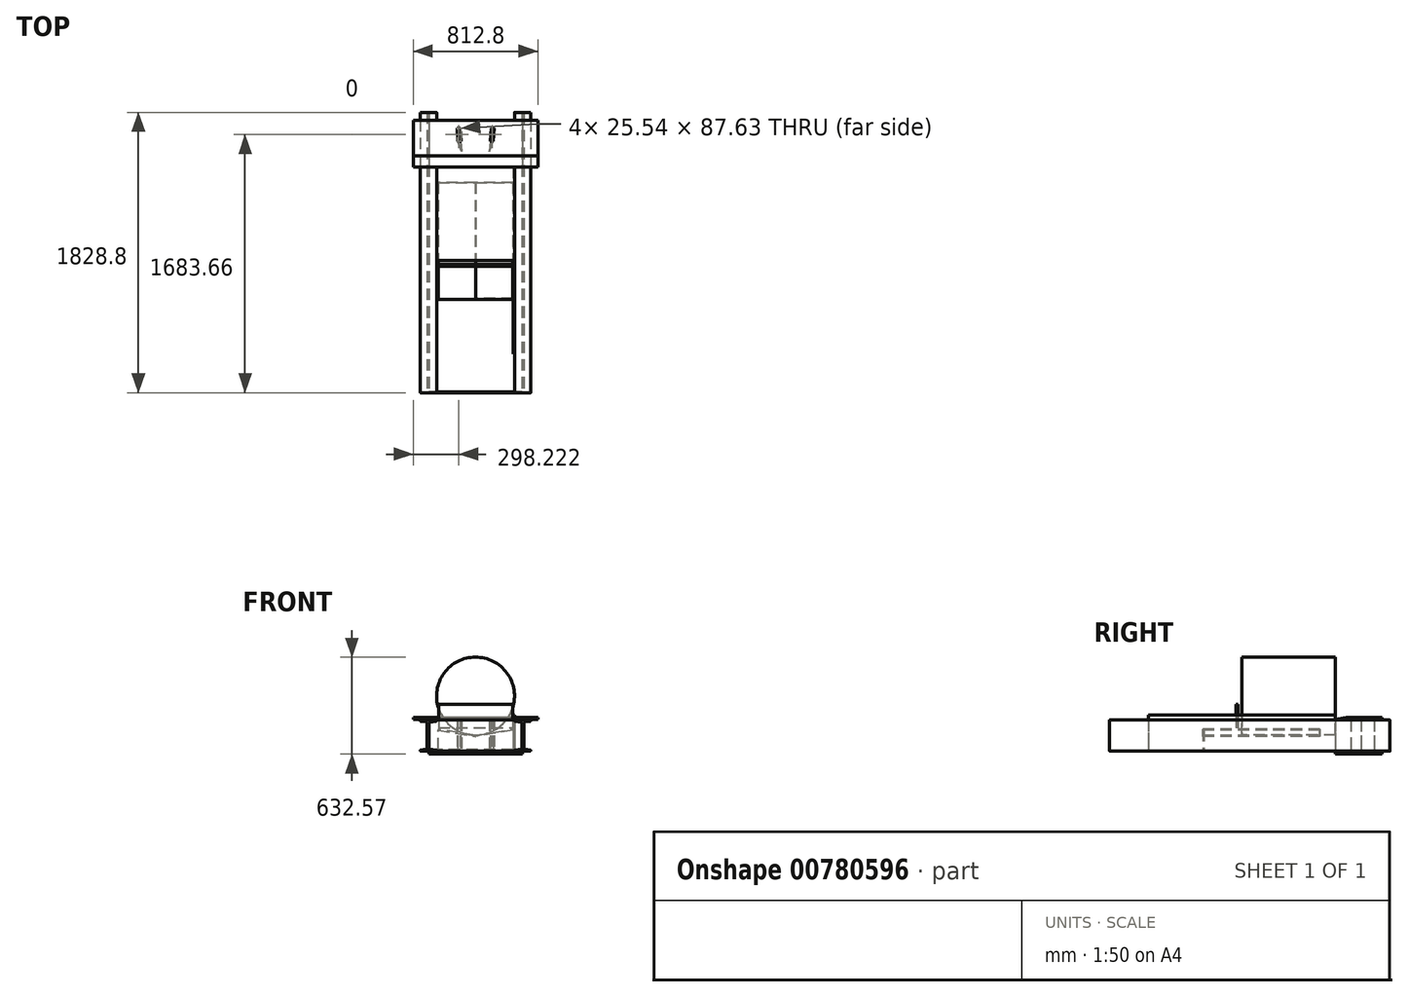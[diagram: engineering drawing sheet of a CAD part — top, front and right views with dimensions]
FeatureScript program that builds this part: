
annotation { "Feature Type Name" : "Feature", "Feature Type Description" : "" }
export const myFeature = defineFeature(function(context is Context, id is Id, definition is map)
    precondition{}
    {
        {
            var Q0;
            Q0=qCreatedBy(makeId("Front.planeOp"),FACE);
            var sketch = newSketch(context, id + "F0", { "sketchPlane" : qUnion([Q0])});
            skLineSegment(sketch, "E0", {"start": v(-357.5, -203.2) * mm, "end": v(-257.18, -203.2) * mm});
            skLineSegment(sketch, "E1", {"start": v(-357.5, 0) * mm, "end": v(-257.18, 0) * mm});
            skLineSegment(sketch, "E2", {"start": v(-360.68, -3.18) * mm, "end": v(-360.68, -5.19) * mm});
            skLineSegment(sketch, "E3", {"start": v(-254, -3.18) * mm, "end": v(-254, -5.15) * mm});
            skLineSegment(sketch, "E4", {"start": v(-256.76, -8.3) * mm, "end": v(-296.95, -13.6) * mm});
            skLineSegment(sketch, "E5", {"start": v(-303.86, -21.46) * mm, "end": v(-303.86, -181.82) * mm});
            skLineSegment(sketch, "E6", {"start": v(-297.05, -189.68) * mm, "end": v(-256.72, -195.5) * mm});
            skLineSegment(sketch, "E7", {"start": v(-254, -198.63) * mm, "end": v(-254, -200.03) * mm});
            skLineSegment(sketch, "E8", {"start": v(-360.68, -200.03) * mm, "end": v(-360.68, -198.6) * mm});
            skLineSegment(sketch, "E9", {"start": v(-358, -195.46) * mm, "end": v(-321.83, -189.76) * mm});
            skLineSegment(sketch, "E10", {"start": v(-315.13, -181.92) * mm, "end": v(-315.13, -21.38) * mm});
            skLineSegment(sketch, "E11", {"start": v(-321.94, -13.52) * mm, "end": v(-357.96, -8.33) * mm});
            skPoint(sketch, "E12.visualSharp", {"position": v(-360.68, -7.94) * mm});
            skArc(sketch, "E12.filletArc", {"start": v(-360.68, -5.19) * mm, "mid": v(-359.9, -7.27) * mm, "end": v(-357.96, -8.33) * mm});
            skPoint(sketch, "E13.visualSharp", {"position": v(-360.68, -195.88) * mm});
            skArc(sketch, "E13.filletArc", {"start": v(-358, -195.46) * mm, "mid": v(-359.92, -196.53) * mm, "end": v(-360.68, -198.6) * mm});
            skPoint(sketch, "E14.visualSharp", {"position": v(-254, -7.94) * mm});
            skArc(sketch, "E14.filletArc", {"start": v(-256.76, -8.3) * mm, "mid": v(-254.79, -7.25) * mm, "end": v(-254, -5.15) * mm});
            skPoint(sketch, "E15.visualSharp", {"position": v(-254, -195.88) * mm});
            skArc(sketch, "E15.filletArc", {"start": v(-254, -198.63) * mm, "mid": v(-254.78, -196.55) * mm, "end": v(-256.72, -195.5) * mm});
            skPoint(sketch, "E16.visualSharp", {"position": v(-254, -203.2) * mm});
            skArc(sketch, "E16.filletArc", {"start": v(-257.18, -203.2) * mm, "mid": v(-254.93, -202.27) * mm, "end": v(-254, -200.03) * mm});
            skPoint(sketch, "E17.visualSharp", {"position": v(-360.68, -203.2) * mm});
            skArc(sketch, "E17.filletArc", {"start": v(-360.68, -200.03) * mm, "mid": v(-359.75, -202.27) * mm, "end": v(-357.5, -203.2) * mm});
            skPoint(sketch, "E18.visualSharp", {"position": v(-360.68, 0) * mm});
            skArc(sketch, "E18.filletArc", {"start": v(-357.5, 0) * mm, "mid": v(-359.75, -0.93) * mm, "end": v(-360.68, -3.18) * mm});
            skPoint(sketch, "E19.visualSharp", {"position": v(-254, 0) * mm});
            skArc(sketch, "E19.filletArc", {"start": v(-254, -3.18) * mm, "mid": v(-254.93, -0.93) * mm, "end": v(-257.18, 0) * mm});
            skPoint(sketch, "E20.visualSharp", {"position": v(-303.86, -14.5) * mm});
            skArc(sketch, "E20.filletArc", {"start": v(-296.95, -13.6) * mm, "mid": v(-301.89, -16.23) * mm, "end": v(-303.86, -21.46) * mm});
            skPoint(sketch, "E21.visualSharp", {"position": v(-315.13, -14.5) * mm});
            skArc(sketch, "E21.filletArc", {"start": v(-315.13, -21.38) * mm, "mid": v(-317.07, -16.18) * mm, "end": v(-321.94, -13.52) * mm});
            skPoint(sketch, "E22.visualSharp", {"position": v(-303.86, -188.7) * mm});
            skArc(sketch, "E22.filletArc", {"start": v(-303.86, -181.82) * mm, "mid": v(-301.92, -187.02) * mm, "end": v(-297.05, -189.68) * mm});
            skPoint(sketch, "E23.visualSharp", {"position": v(-315.13, -188.7) * mm});
            skArc(sketch, "E23.filletArc", {"start": v(-321.83, -189.76) * mm, "mid": v(-317.04, -187.07) * mm, "end": v(-315.13, -181.92) * mm});
            skSolve(sketch);
        }
        {
            var Q0;
            Q0 = qSketchRegion(id + "F0", true);
            extrude(context, id + "F1", {"entities" : qUnion([Q0]), "oppositeDirection" : true, "depth" : 1828.8 * mm, "offsetDistance" : 25.4 * mm});
        }
        {
            var Q0;
            Q0=makeQuery(id+"F1.opExtrude","SWEPT_BODY",BODY,{"disambiguationData":[OSD([sQuery(id+"F0.wireOp",EDGE,"E0"),sQuery(id+"F0.wireOp",EDGE,"E1"),sQuery(id+"F0.wireOp",EDGE,"E2"),sQuery(id+"F0.wireOp",EDGE,"E3"),sQuery(id+"F0.wireOp",EDGE,"E4"),sQuery(id+"F0.wireOp",EDGE,"E5"),sQuery(id+"F0.wireOp",EDGE,"E6"),sQuery(id+"F0.wireOp",EDGE,"E7"),sQuery(id+"F0.wireOp",EDGE,"E8"),sQuery(id+"F0.wireOp",EDGE,"E9"),sQuery(id+"F0.wireOp",EDGE,"E10"),sQuery(id+"F0.wireOp",EDGE,"E11"),sQuery(id+"F0.wireOp",EDGE,"E12.filletArc"),sQuery(id+"F0.wireOp",EDGE,"E13.filletArc"),sQuery(id+"F0.wireOp",EDGE,"E14.filletArc"),sQuery(id+"F0.wireOp",EDGE,"E15.filletArc"),sQuery(id+"F0.wireOp",EDGE,"E16.filletArc"),sQuery(id+"F0.wireOp",EDGE,"E17.filletArc"),sQuery(id+"F0.wireOp",EDGE,"E18.filletArc"),sQuery(id+"F0.wireOp",EDGE,"E19.filletArc"),sQuery(id+"F0.wireOp",EDGE,"E20.filletArc"),sQuery(id+"F0.wireOp",EDGE,"E21.filletArc"),sQuery(id+"F0.wireOp",EDGE,"E22.filletArc"),sQuery(id+"F0.wireOp",EDGE,"E23.filletArc")])]});
            var Q1;
            Q1=qCreatedBy(makeId("Right.planeOp"),FACE);
            mirror(context, id + "F2", {"entities" : qUnion([Q0]), "mirrorPlane" : qUnion([Q1])});
        }
        {
            var Q0;
            Q0=qCreatedBy(makeId("Front.planeOp"),FACE);
            var sketch = newSketch(context, id + "F3", { "sketchPlane" : qUnion([Q0])});
            skLineSegment(sketch, "E24.bottom", {"start": v(-303.86, -203.2) * mm, "end": v(303.86, -203.2) * mm});
            skLineSegment(sketch, "E24.top", {"start": v(-303.86, 0) * mm, "end": v(303.86, 0) * mm});
            skLineSegment(sketch, "E24.left", {"start": v(-303.86, -203.2) * mm, "end": v(-303.86, 0) * mm});
            skLineSegment(sketch, "E24.right", {"start": v(303.86, -203.2) * mm, "end": v(303.86, 0) * mm});
            skSolve(sketch);
        }
        {
            var Q0;
            Q0=makeQuery(id+"F3.imprint","IMPRINT",FACE,{"disambiguationData":[TD([[makeQuery(id+"F3.imprint","IMPRINT",EDGE,{"derivedFrom":sQuery(id+"F3.wireOp",EDGE,"E24.bottom")}),1.0]])]});
            extrude(context, id + "F4", {"entities" : qUnion([Q0]), "oppositeDirection" : true, "depth" : 6.35 * mm, "offsetDistance" : 25.4 * mm});
        }
        {
            var Q0;
            Q0=makeQuery(id+"F1.opExtrude","SWEPT_BODY",BODY,{"disambiguationData":[OSD([sQuery(id+"F0.wireOp",EDGE,"E0"),sQuery(id+"F0.wireOp",EDGE,"E1"),sQuery(id+"F0.wireOp",EDGE,"E2"),sQuery(id+"F0.wireOp",EDGE,"E3"),sQuery(id+"F0.wireOp",EDGE,"E4"),sQuery(id+"F0.wireOp",EDGE,"E5"),sQuery(id+"F0.wireOp",EDGE,"E6"),sQuery(id+"F0.wireOp",EDGE,"E7"),sQuery(id+"F0.wireOp",EDGE,"E8"),sQuery(id+"F0.wireOp",EDGE,"E9"),sQuery(id+"F0.wireOp",EDGE,"E10"),sQuery(id+"F0.wireOp",EDGE,"E11"),sQuery(id+"F0.wireOp",EDGE,"E12.filletArc"),sQuery(id+"F0.wireOp",EDGE,"E13.filletArc"),sQuery(id+"F0.wireOp",EDGE,"E14.filletArc"),sQuery(id+"F0.wireOp",EDGE,"E15.filletArc"),sQuery(id+"F0.wireOp",EDGE,"E16.filletArc"),sQuery(id+"F0.wireOp",EDGE,"E17.filletArc"),sQuery(id+"F0.wireOp",EDGE,"E18.filletArc"),sQuery(id+"F0.wireOp",EDGE,"E19.filletArc"),sQuery(id+"F0.wireOp",EDGE,"E20.filletArc"),sQuery(id+"F0.wireOp",EDGE,"E21.filletArc"),sQuery(id+"F0.wireOp",EDGE,"E22.filletArc"),sQuery(id+"F0.wireOp",EDGE,"E23.filletArc")])]});
            var Q1;
            Q1=makeQuery(id+"F2.opPattern","COPY",BODY,{"derivedFrom":makeQuery(id+"F1.opExtrude","SWEPT_BODY",BODY,{"disambiguationData":[OSD([sQuery(id+"F0.wireOp",EDGE,"E0"),sQuery(id+"F0.wireOp",EDGE,"E1"),sQuery(id+"F0.wireOp",EDGE,"E2"),sQuery(id+"F0.wireOp",EDGE,"E3"),sQuery(id+"F0.wireOp",EDGE,"E4"),sQuery(id+"F0.wireOp",EDGE,"E5"),sQuery(id+"F0.wireOp",EDGE,"E6"),sQuery(id+"F0.wireOp",EDGE,"E7"),sQuery(id+"F0.wireOp",EDGE,"E8"),sQuery(id+"F0.wireOp",EDGE,"E9"),sQuery(id+"F0.wireOp",EDGE,"E10"),sQuery(id+"F0.wireOp",EDGE,"E11"),sQuery(id+"F0.wireOp",EDGE,"E12.filletArc"),sQuery(id+"F0.wireOp",EDGE,"E13.filletArc"),sQuery(id+"F0.wireOp",EDGE,"E14.filletArc"),sQuery(id+"F0.wireOp",EDGE,"E15.filletArc"),sQuery(id+"F0.wireOp",EDGE,"E16.filletArc"),sQuery(id+"F0.wireOp",EDGE,"E17.filletArc"),sQuery(id+"F0.wireOp",EDGE,"E18.filletArc"),sQuery(id+"F0.wireOp",EDGE,"E19.filletArc"),sQuery(id+"F0.wireOp",EDGE,"E20.filletArc"),sQuery(id+"F0.wireOp",EDGE,"E21.filletArc"),sQuery(id+"F0.wireOp",EDGE,"E22.filletArc"),sQuery(id+"F0.wireOp",EDGE,"E23.filletArc")])]}),"instanceName":"1"});
            var Q2;
            Q2=makeQuery(id+"F4.opExtrude","SWEPT_BODY",BODY,{"disambiguationData":[OSD([sQuery(id+"F3.wireOp",EDGE,"E24.bottom"),sQuery(id+"F3.wireOp",EDGE,"E24.top"),sQuery(id+"F3.wireOp",EDGE,"E24.left"),sQuery(id+"F3.wireOp",EDGE,"E24.right")])]});
            var Q3;
            Q3=makeQuery(id+"F1.opExtrude","SWEPT_FACE",FACE,{"disambiguationData":[OSD([sQuery(id+"F0.wireOp",EDGE,"E19.filletArc")])]});
            var Q4;
            Q4=makeQuery(id+"F1.opExtrude","SWEPT_FACE",FACE,{"disambiguationData":[OSD([sQuery(id+"F0.wireOp",EDGE,"E1")])]});
            var Q5;
            Q5=makeQuery(id+"F1.opExtrude","SWEPT_FACE",FACE,{"disambiguationData":[OSD([sQuery(id+"F0.wireOp",EDGE,"E3")])]});
            var Q6;
            Q6=makeQuery(id+"F1.opExtrude","SWEPT_FACE",FACE,{"disambiguationData":[OSD([sQuery(id+"F0.wireOp",EDGE,"E14.filletArc")])]});
            var Q7;
            Q7=makeQuery(id+"F1.opExtrude","SWEPT_FACE",FACE,{"disambiguationData":[OSD([sQuery(id+"F0.wireOp",EDGE,"E4")])]});
            var Q8;
            Q8=makeQuery(id+"F1.opExtrude","SWEPT_FACE",FACE,{"disambiguationData":[OSD([sQuery(id+"F0.wireOp",EDGE,"E20.filletArc")])]});
            var Q9;
            Q9=makeQuery(id+"F1.opExtrude","SWEPT_FACE",FACE,{"disambiguationData":[OSD([sQuery(id+"F0.wireOp",EDGE,"E5")])]});
            var Q10;
            Q10=makeQuery(id+"F1.opExtrude","SWEPT_FACE",FACE,{"disambiguationData":[OSD([sQuery(id+"F0.wireOp",EDGE,"E22.filletArc")])]});
            var Q11;
            Q11=makeQuery(id+"F1.opExtrude","SWEPT_FACE",FACE,{"disambiguationData":[OSD([sQuery(id+"F0.wireOp",EDGE,"E6")])]});
            var Q12;
            Q12=makeQuery(id+"F1.opExtrude","SWEPT_FACE",FACE,{"disambiguationData":[OSD([sQuery(id+"F0.wireOp",EDGE,"E15.filletArc")])]});
            var Q13;
            Q13=makeQuery(id+"F1.opExtrude","SWEPT_FACE",FACE,{"disambiguationData":[OSD([sQuery(id+"F0.wireOp",EDGE,"E7")])]});
            var Q14;
            Q14=makeQuery(id+"F1.opExtrude","SWEPT_FACE",FACE,{"disambiguationData":[OSD([sQuery(id+"F0.wireOp",EDGE,"E16.filletArc")])]});
            var Q15;
            Q15=makeQuery(id+"F1.opExtrude","SWEPT_FACE",FACE,{"disambiguationData":[OSD([sQuery(id+"F0.wireOp",EDGE,"E0")])]});
            var Q16;
            Q16=makeQuery(id+"F2.opPattern","COPY",FACE,{"derivedFrom":makeQuery(id+"F1.opExtrude","SWEPT_FACE",FACE,{"disambiguationData":[OSD([sQuery(id+"F0.wireOp",EDGE,"E1")])]}),"instanceName":"1"});
            var Q17;
            Q17=makeQuery(id+"F2.opPattern","COPY",FACE,{"derivedFrom":makeQuery(id+"F1.opExtrude","SWEPT_FACE",FACE,{"disambiguationData":[OSD([sQuery(id+"F0.wireOp",EDGE,"E19.filletArc")])]}),"instanceName":"1"});
            var Q18;
            Q18=makeQuery(id+"F2.opPattern","COPY",FACE,{"derivedFrom":makeQuery(id+"F1.opExtrude","SWEPT_FACE",FACE,{"disambiguationData":[OSD([sQuery(id+"F0.wireOp",EDGE,"E3")])]}),"instanceName":"1"});
            var Q19;
            Q19=makeQuery(id+"F2.opPattern","COPY",FACE,{"derivedFrom":makeQuery(id+"F1.opExtrude","SWEPT_FACE",FACE,{"disambiguationData":[OSD([sQuery(id+"F0.wireOp",EDGE,"E14.filletArc")])]}),"instanceName":"1"});
            var Q20;
            Q20=makeQuery(id+"F2.opPattern","COPY",FACE,{"derivedFrom":makeQuery(id+"F1.opExtrude","SWEPT_FACE",FACE,{"disambiguationData":[OSD([sQuery(id+"F0.wireOp",EDGE,"E4")])]}),"instanceName":"1"});
            var Q21;
            Q21=makeQuery(id+"F2.opPattern","COPY",FACE,{"derivedFrom":makeQuery(id+"F1.opExtrude","SWEPT_FACE",FACE,{"disambiguationData":[OSD([sQuery(id+"F0.wireOp",EDGE,"E20.filletArc")])]}),"instanceName":"1"});
            var Q22;
            Q22=makeQuery(id+"F2.opPattern","COPY",FACE,{"derivedFrom":makeQuery(id+"F1.opExtrude","SWEPT_FACE",FACE,{"disambiguationData":[OSD([sQuery(id+"F0.wireOp",EDGE,"E5")])]}),"instanceName":"1"});
            var Q23;
            Q23=makeQuery(id+"F2.opPattern","COPY",FACE,{"derivedFrom":makeQuery(id+"F1.opExtrude","SWEPT_FACE",FACE,{"disambiguationData":[OSD([sQuery(id+"F0.wireOp",EDGE,"E22.filletArc")])]}),"instanceName":"1"});
            var Q24;
            Q24=makeQuery(id+"F2.opPattern","COPY",FACE,{"derivedFrom":makeQuery(id+"F1.opExtrude","SWEPT_FACE",FACE,{"disambiguationData":[OSD([sQuery(id+"F0.wireOp",EDGE,"E6")])]}),"instanceName":"1"});
            var Q25;
            Q25=makeQuery(id+"F2.opPattern","COPY",FACE,{"derivedFrom":makeQuery(id+"F1.opExtrude","SWEPT_FACE",FACE,{"disambiguationData":[OSD([sQuery(id+"F0.wireOp",EDGE,"E15.filletArc")])]}),"instanceName":"1"});
            var Q26;
            Q26=makeQuery(id+"F2.opPattern","COPY",FACE,{"derivedFrom":makeQuery(id+"F1.opExtrude","SWEPT_FACE",FACE,{"disambiguationData":[OSD([sQuery(id+"F0.wireOp",EDGE,"E7")])]}),"instanceName":"1"});
            var Q27;
            Q27=makeQuery(id+"F2.opPattern","COPY",FACE,{"derivedFrom":makeQuery(id+"F1.opExtrude","SWEPT_FACE",FACE,{"disambiguationData":[OSD([sQuery(id+"F0.wireOp",EDGE,"E16.filletArc")])]}),"instanceName":"1"});
            var Q28;
            Q28=makeQuery(id+"F2.opPattern","COPY",FACE,{"derivedFrom":makeQuery(id+"F1.opExtrude","SWEPT_FACE",FACE,{"disambiguationData":[OSD([sQuery(id+"F0.wireOp",EDGE,"E0")])]}),"instanceName":"1"});
            booleanBodies(context, id + "F5", {"operationType" : BooleanOperationType.SUBTRACTION, "tools" : qUnion([Q0, Q1]), "targets" : qUnion([Q2]), "offset" : true, "entitiesToOffset" : qUnion([Q3, Q4, Q5, Q6, Q7, Q8, Q9, Q10, Q11, Q12, Q13, Q14, Q15, Q16, Q17, Q18, Q19, Q20, Q21, Q22, Q23, Q24, Q25, Q26, Q27, Q28]), "offsetDistance" : 0.25 * mm, "keepTools" : true});
        }
        {
            var Q0;
            Q0=qCreatedBy(makeId("Right.planeOp"),FACE);
            var sketch = newSketch(context, id + "F6", { "sketchPlane" : qUnion([Q0])});
            skLineSegment(sketch, "E25", {"start": v(1778, 15.24) * mm, "end": v(1778, 2.54) * mm});
            skLineSegment(sketch, "E26", {"start": v(1778, 2.54) * mm, "end": v(1473.2, 2.54) * mm});
            skLineSegment(sketch, "E27", {"start": v(1473.2, 2.54) * mm, "end": v(1545.23, 15.24) * mm});
            skLineSegment(sketch, "E28", {"start": v(1545.23, 15.24) * mm, "end": v(1778, 15.24) * mm});
            skSolve(sketch);
        }
        {
            var Q0;
            Q0=makeQuery(id+"F6.imprint","IMPRINT",FACE,{"disambiguationData":[TD([[makeQuery(id+"F6.imprint","IMPRINT",EDGE,{"derivedFrom":sQuery(id+"F6.wireOp",EDGE,"E25")}),-1.0]])]});
            extrude(context, id + "F7", {"entities" : qUnion([Q0]), "depth" : 406.4 * mm, "offsetDistance" : 25.4 * mm, "hasSecondDirection" : true, "secondDirectionOppositeDirection" : true, "secondDirectionDepth" : 406.4 * mm});
        }
        {
            var Q0;
            Q0=qCreatedBy(makeId("Right.planeOp"),FACE);
            var sketch = newSketch(context, id + "F8", { "sketchPlane" : qUnion([Q0])});
            skLineSegment(sketch, "E29.bottom", {"start": v(1778, -203.2) * mm, "end": v(1473.2, -203.2) * mm});
            skLineSegment(sketch, "E29.top", {"start": v(1778, -222.25) * mm, "end": v(1473.2, -222.25) * mm});
            skLineSegment(sketch, "E29.left", {"start": v(1778, -203.2) * mm, "end": v(1778, -222.25) * mm});
            skLineSegment(sketch, "E29.right", {"start": v(1473.2, -203.2) * mm, "end": v(1473.2, -222.25) * mm});
            skSolve(sketch);
        }
        {
            var Q0;
            Q0=qCreatedBy(makeId("Front.planeOp"),FACE);
            var sketch = newSketch(context, id + "F9", { "sketchPlane" : qUnion([Q0])});
            skLineSegment(sketch, "E30.top", {"start": v(254, -203.2) * mm, "end": v(244.48, -203.2) * mm});
            skLineSegment(sketch, "E30.left", {"start": v(254, 0) * mm, "end": v(254, -203.2) * mm});
            skLineSegment(sketch, "E30.right", {"start": v(244.48, 31.75) * mm, "end": v(244.48, -203.2) * mm});
            skLineSegment(sketch, "E31", {"start": v(244.47, 31.75) * mm, "end": v(254, 31.75) * mm});
            skLineSegment(sketch, "E32", {"start": v(254, 31.75) * mm, "end": v(254, 0) * mm});
            skSolve(sketch);
        }
        {
            var Q0;
            Q0=makeQuery(id+"F8.imprint","IMPRINT",FACE,{"disambiguationData":[TD([[makeQuery(id+"F8.imprint","IMPRINT",EDGE,{"derivedFrom":sQuery(id+"F8.wireOp",EDGE,"E29.bottom")}),1.0]])]});
            extrude(context, id + "F10", {"entities" : qUnion([Q0]), "depth" : 304.8 * mm, "offsetDistance" : 25.4 * mm, "hasSecondDirection" : true, "secondDirectionOppositeDirection" : true, "secondDirectionDepth" : 304.8 * mm});
        }
        {
            var Q0;
            Q0=qCreatedBy(makeId("Front.planeOp"),FACE);
            var sketch = newSketch(context, id + "F11", { "sketchPlane" : qUnion([Q0])});
            skLineSegment(sketch, "E33", {"start": v(243.37, -58.69) * mm, "end": v(244.47, -64.94) * mm});
            skLineSegment(sketch, "E34", {"start": v(244.48, -64.94) * mm, "end": v(1.1, -107.85) * mm});
            skLineSegment(sketch, "E35", {"start": v(1.1, -107.85) * mm, "end": v(0, -101.6) * mm});
            skLineSegment(sketch, "E36", {"start": v(0, -101.6) * mm, "end": v(243.37, -58.69) * mm});
            skSolve(sketch);
        }
        {
            var Q0;
            Q0 = qSketchRegion(id + "F11", true);
            extrude(context, id + "F12", {"entities" : qUnion([Q0]), "oppositeDirection" : true, "depth" : 1371.6 * mm, "offsetDistance" : 25.4 * mm, "hasSecondDirection" : true, "secondDirectionOppositeDirection" : true, "secondDirectionDepth" : 609.6 * mm});
        }
        {
            var Q0;
            Q0=makeQuery(id+"F12.opExtrude","SWEPT_BODY",BODY,{"disambiguationData":[OSD([sQuery(id+"F11.wireOp",EDGE,"E33"),sQuery(id+"F11.wireOp",EDGE,"E34"),sQuery(id+"F11.wireOp",EDGE,"E35"),sQuery(id+"F11.wireOp",EDGE,"E36")])]});
            var Q1;
            Q1=qCreatedBy(makeId("Right.planeOp"),FACE);
            mirror(context, id + "F13", {"entities" : qUnion([Q0]), "mirrorPlane" : qUnion([Q1])});
        }
        {
            var Q0;
            Q0=makeQuery(id+"F12.opExtrude","CAP_FACE",FACE,{"disambiguationData":[OSD([sQuery(id+"F11.wireOp",EDGE,"E33"),sQuery(id+"F11.wireOp",EDGE,"E34"),sQuery(id+"F11.wireOp",EDGE,"E35"),sQuery(id+"F11.wireOp",EDGE,"E36")])],"isStart":true});
            var sketch = newSketch(context, id + "F14", { "sketchPlane" : qUnion([Q0])});
            skLineSegment(sketch, "E37", {"start": v(244.47, -64.94) * mm, "end": v(244.47, -191.94) * mm});
            skLineSegment(sketch, "E38", {"start": v(244.47, -191.94) * mm, "end": v(-244.47, -191.94) * mm});
            skLineSegment(sketch, "E39", {"start": v(-244.47, -191.94) * mm, "end": v(-244.47, -64.94) * mm});
            skLineSegment(sketch, "E40", {"start": v(-244.47, -64.94) * mm, "end": v(0, -108.05) * mm});
            skLineSegment(sketch, "E41", {"start": v(0, -108.05) * mm, "end": v(244.48, -64.94) * mm});
            skSolve(sketch);
        }
        {
            var Q0;
            Q0 = qSketchRegion(id + "F14", true);
            extrude(context, id + "F15", {"entities" : qUnion([Q0]), "oppositeDirection" : true, "depth" : 6.35 * mm, "offsetDistance" : 25.4 * mm});
        }
        {
            var Q0;
            Q0=makeQuery(id+"F13.opPattern","COPY",FACE,{"derivedFrom":makeQuery(id+"F12.opExtrude","CAP_FACE",FACE,{"disambiguationData":[OSD([sQuery(id+"F11.wireOp",EDGE,"E33"),sQuery(id+"F11.wireOp",EDGE,"E34"),sQuery(id+"F11.wireOp",EDGE,"E35"),sQuery(id+"F11.wireOp",EDGE,"E36")])],"isStart":false}),"instanceName":"1"});
            var sketch = newSketch(context, id + "F16", { "sketchPlane" : qUnion([Q0])});
            skCircle(sketch, "E42", {"center": v(0, 156.32) * mm, "radius": 254 * mm});
            skSolve(sketch);
        }
        {
            var Q0;
            Q0=qCreatedBy(makeId("Top.planeOp"),FACE);
            var sketch = newSketch(context, id + "F17", { "sketchPlane" : qUnion([Q0])});
            skLineSegment(sketch, "E43", {"start": v(91.04, 1575.17) * mm, "end": v(101.67, 1727.2) * mm});
            skLineSegment(sketch, "E44", {"start": v(101.67, 1727.2) * mm, "end": v(120.68, 1725.87) * mm});
            skLineSegment(sketch, "E45", {"start": v(120.68, 1725.87) * mm, "end": v(114.68, 1640.12) * mm});
            skLineSegment(sketch, "E46", {"start": v(114.68, 1640.12) * mm, "end": v(91.04, 1575.17) * mm});
            skLineSegment(sketch, "E47", {"start": v(114.68, 1640.12) * mm, "end": v(95.68, 1641.44) * mm});
            skSolve(sketch);
        }
        {
            var Q0;
            {var subQ0=sQuery(id+"F17.wireOp",EDGE,"E44");Q0=makeQuery(id+"F17.imprint","IMPRINT",FACE,{"disambiguationData":[TD([[makeQuery(id+"F17.imprint","IMPRINT",EDGE,{"derivedFrom":subQ0}),-1.0]])]});}
            var Q1;
            Q1=makeQuery(id+"F7.opExtrude","SWEPT_FACE",FACE,{"disambiguationData":[OSD([sQuery(id+"F6.wireOp",EDGE,"E28")])]});
            var Q2;
            Q2=makeQuery(id+"F10.opExtrude","SWEPT_FACE",FACE,{"disambiguationData":[OSD([sQuery(id+"F8.wireOp",EDGE,"E29.top")])]});
            extrude(context, id + "F18", {"entities" : qUnion([Q0]), "endBound" : BoundingType.UP_TO_SURFACE, "depth" : 25.4 * mm, "endBoundEntityFace" : qUnion([Q1]), "offsetDistance" : 25.4 * mm, "hasSecondDirection" : true, "secondDirectionBound" : SecondDirectionBoundingType.UP_TO_SURFACE, "secondDirectionOppositeDirection" : true, "secondDirectionDepth" : 25.4 * mm, "secondDirectionBoundEntityFace" : qUnion([Q2])});
        }
        {
            var Q0;
            {var subQ0=sQuery(id+"F17.wireOp",EDGE,"E46");Q0=makeQuery(id+"F17.imprint","IMPRINT",FACE,{"disambiguationData":[TD([[makeQuery(id+"F17.imprint","IMPRINT",EDGE,{"derivedFrom":subQ0}),-1.0]])]});}
            var Q1;
            Q1=makeQuery(id+"F7.opExtrude","SWEPT_FACE",FACE,{"disambiguationData":[OSD([sQuery(id+"F6.wireOp",EDGE,"E26")])]});
            var Q2;
            Q2=makeQuery(id+"F10.opExtrude","SWEPT_FACE",FACE,{"disambiguationData":[OSD([sQuery(id+"F8.wireOp",EDGE,"E29.bottom")])]});
            extrude(context, id + "F19", {"entities" : qUnion([Q0]), "endBound" : BoundingType.UP_TO_SURFACE, "depth" : 25.4 * mm, "endBoundEntityFace" : qUnion([Q1]), "offsetDistance" : 25.4 * mm, "hasSecondDirection" : true, "secondDirectionBound" : SecondDirectionBoundingType.UP_TO_SURFACE, "secondDirectionOppositeDirection" : true, "secondDirectionDepth" : 25.4 * mm, "secondDirectionBoundEntityFace" : qUnion([Q2])});
        }
        {
            var Q0;
            Q0=makeQuery(id+"F18.opExtrude","SWEPT_BODY",BODY,{"disambiguationData":[OSD([sQuery(id+"F17.wireOp",EDGE,"E43"),sQuery(id+"F17.wireOp",EDGE,"E44"),sQuery(id+"F17.wireOp",EDGE,"E45"),sQuery(id+"F17.wireOp",EDGE,"E47")])]});
            var Q1;
            Q1=qCreatedBy(makeId("Right.planeOp"),FACE);
            mirror(context, id + "F20", {"entities" : qUnion([Q0]), "mirrorPlane" : qUnion([Q1])});
        }
        {
            var Q0;
            Q0=makeQuery(id+"F20.opPattern","COPY",BODY,{"derivedFrom":makeQuery(id+"F18.opExtrude","SWEPT_BODY",BODY,{"disambiguationData":[OSD([sQuery(id+"F17.wireOp",EDGE,"E43"),sQuery(id+"F17.wireOp",EDGE,"E44"),sQuery(id+"F17.wireOp",EDGE,"E45"),sQuery(id+"F17.wireOp",EDGE,"E47")])]}),"instanceName":"1"});
            var Q1;
            Q1=makeQuery(id+"F18.opExtrude","SWEPT_BODY",BODY,{"disambiguationData":[OSD([sQuery(id+"F17.wireOp",EDGE,"E43"),sQuery(id+"F17.wireOp",EDGE,"E44"),sQuery(id+"F17.wireOp",EDGE,"E45"),sQuery(id+"F17.wireOp",EDGE,"E47")])]});
            var Q2;
            Q2=makeQuery(id+"F7.opExtrude","SWEPT_BODY",BODY,{"disambiguationData":[OSD([sQuery(id+"F6.wireOp",EDGE,"E25"),sQuery(id+"F6.wireOp",EDGE,"E26"),sQuery(id+"F6.wireOp",EDGE,"E27"),sQuery(id+"F6.wireOp",EDGE,"E28")])]});
            var Q3;
            Q3=makeQuery(id+"F10.opExtrude","SWEPT_BODY",BODY,{"disambiguationData":[OSD([sQuery(id+"F8.wireOp",EDGE,"E29.bottom"),sQuery(id+"F8.wireOp",EDGE,"E29.top"),sQuery(id+"F8.wireOp",EDGE,"E29.left"),sQuery(id+"F8.wireOp",EDGE,"E29.right")])]});
            booleanBodies(context, id + "F21", {"operationType" : BooleanOperationType.SUBTRACTION, "tools" : qUnion([Q0, Q1]), "targets" : qUnion([Q2, Q3]), "offset" : true, "offsetAll" : true, "offsetDistance" : 0.25 * mm, "keepTools" : true});
        }
        {
            var Q0;
            Q0=makeQuery(id+"F19.opExtrude","SWEPT_BODY",BODY,{"disambiguationData":[OSD([sQuery(id+"F17.wireOp",EDGE,"E43"),sQuery(id+"F17.wireOp",EDGE,"E46"),sQuery(id+"F17.wireOp",EDGE,"E47")])]});
            var Q1;
            Q1=qCreatedBy(makeId("Right.planeOp"),FACE);
            mirror(context, id + "F22", {"entities" : qUnion([Q0]), "mirrorPlane" : qUnion([Q1])});
        }
        {
            var Q0;
            Q0 = qSketchRegion(id + "F9", true);
            extrude(context, id + "F23", {"entities" : qUnion([Q0]), "oppositeDirection" : true, "depth" : 1473.2 * mm, "offsetDistance" : 25.4 * mm, "hasSecondDirection" : true, "secondDirectionOppositeDirection" : true, "secondDirectionDepth" : 254 * mm});
        }
        {
            var Q0;
            Q0 = qSketchRegion(id + "F16", true);
            extrude(context, id + "F24", {"entities" : qUnion([Q0]), "depth" : 101.6 * mm, "offsetDistance" : 25.4 * mm, "hasSecondDirection" : true, "secondDirectionOppositeDirection" : true, "secondDirectionDepth" : 508 * mm});
        }
        {
            var Q0;
            Q0=qCreatedBy(makeId("Front.planeOp"),FACE);
            var sketch = newSketch(context, id + "F25", { "sketchPlane" : qUnion([Q0])});
            skLineSegment(sketch, "E48.bottom", {"start": v(355.6, 0) * mm, "end": v(254, 0) * mm});
            skLineSegment(sketch, "E48.top", {"start": v(355.6, 6.35) * mm, "end": v(254, 6.35) * mm});
            skLineSegment(sketch, "E48.left", {"start": v(355.6, 0) * mm, "end": v(355.6, 6.35) * mm});
            skLineSegment(sketch, "E48.right", {"start": v(254, 0) * mm, "end": v(254, 6.35) * mm});
            skSolve(sketch);
        }
        {
            var Q0;
            Q0=qCreatedBy(makeId("Front.planeOp"),FACE);
            var sketch = newSketch(context, id + "F26", { "sketchPlane" : qUnion([Q0])});
            skLineSegment(sketch, "E49.bottom", {"start": v(279.4, 12.7) * mm, "end": v(355.6, 12.7) * mm});
            skLineSegment(sketch, "E49.top", {"start": v(279.4, 6.35) * mm, "end": v(355.6, 6.35) * mm});
            skLineSegment(sketch, "E49.left", {"start": v(279.4, 12.7) * mm, "end": v(279.4, 6.35) * mm});
            skLineSegment(sketch, "E49.right", {"start": v(355.6, 12.7) * mm, "end": v(355.6, 6.35) * mm});
            skSolve(sketch);
        }
        {
            var Q0;
            Q0=qCreatedBy(makeId("Front.planeOp"),FACE);
            var sketch = newSketch(context, id + "F27", { "sketchPlane" : qUnion([Q0])});
            skLineSegment(sketch, "E50.bottom", {"start": v(-241.3, 101.6) * mm, "end": v(241.3, 101.6) * mm});
            skLineSegment(sketch, "E50.top", {"start": v(-241.3, -50.8) * mm, "end": v(241.3, -50.8) * mm});
            skLineSegment(sketch, "E50.left", {"start": v(-241.3, 101.6) * mm, "end": v(-241.3, -50.8) * mm});
            skLineSegment(sketch, "E50.right", {"start": v(241.3, 101.6) * mm, "end": v(241.3, -50.8) * mm});
            skSolve(sketch);
        }
        {
            var Q0;
            Q0=makeQuery(id+"F27.imprint","IMPRINT",FACE,{"disambiguationData":[TD([[makeQuery(id+"F27.imprint","IMPRINT",EDGE,{"derivedFrom":sQuery(id+"F27.wireOp",EDGE,"E50.bottom")}),-1.0]])]});
            extrude(context, id + "F28", {"entities" : qUnion([Q0]), "oppositeDirection" : true, "depth" : 838.2 * mm, "offsetDistance" : 25.4 * mm, "hasSecondDirection" : true, "secondDirectionOppositeDirection" : true, "secondDirectionDepth" : 825.5 * mm});
        }
    });
